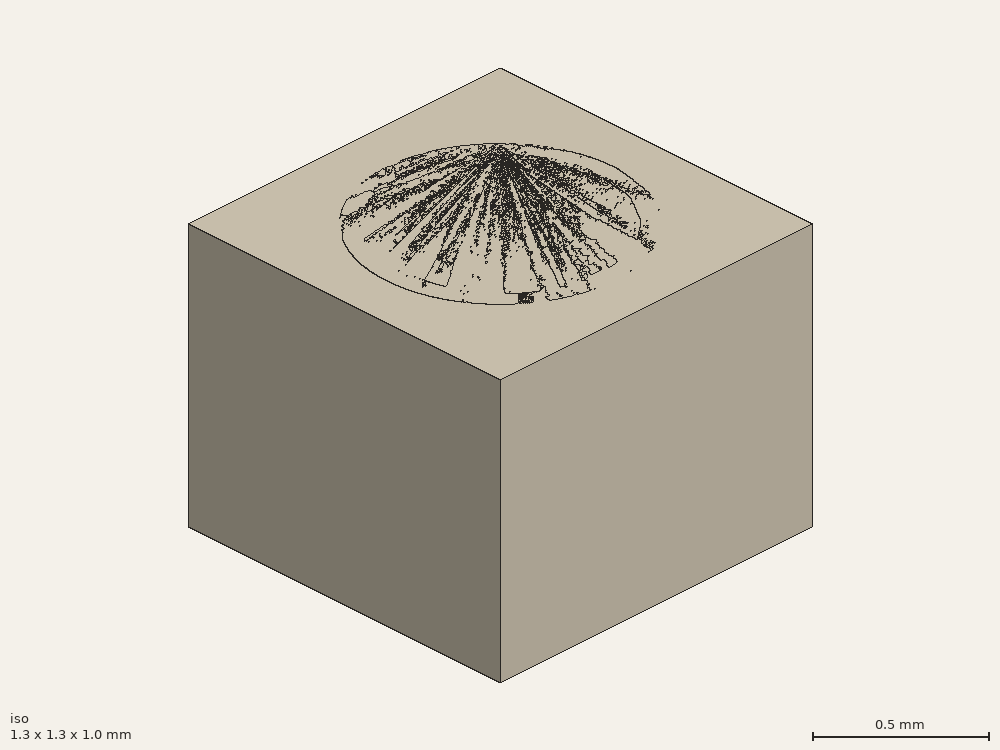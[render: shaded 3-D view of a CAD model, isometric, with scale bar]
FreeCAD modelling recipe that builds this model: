
FCSTD DOCUMENT  (FreeCAD 0.18RUnknown)
Label: PinCellMPACT
License: All rights reserved
LicenseURL: http://en.wikipedia.org/wiki/All_rights_reserved
objects: Part::Cylinder×3, Part::Box×1
note: 4 computed .brp shape members not serialized (recipe doc carries the construction recipe); baked Part::Feature solids carry a one-line shape summary decoded from their .brp

FEATURE [Part::Box] Box  label="water region"
  AttacherType = Attacher::AttachEngine3D
  Height = 1
  Length = 1.26
  Width = 1.26
FEATURE [Part::Cylinder] Cylinder  label="fuel region"
  Angle = 360
  AttacherType = Attacher::AttachEngine3D
  Height = 1
  Placement = pos=(0.63,0.63,0) rot=(0,0,1;0rad)
  Radius = 0.39
FEATURE [Part::Cylinder] Cylinder001  label="clad or"
  Angle = 360
  AttacherType = Attacher::AttachEngine3D
  Height = 1
  Placement = pos=(0.63,0.63,0) rot=(0,0,1;0rad)
  Radius = 0.46
FEATURE [Part::Cylinder] Cylinder002  label="clad ir"
  Angle = 360
  AttacherType = Attacher::AttachEngine3D
  Height = 1
  Placement = pos=(0.63,0.63,0) rot=(0,0,1;0rad)
  Radius = 0.4
